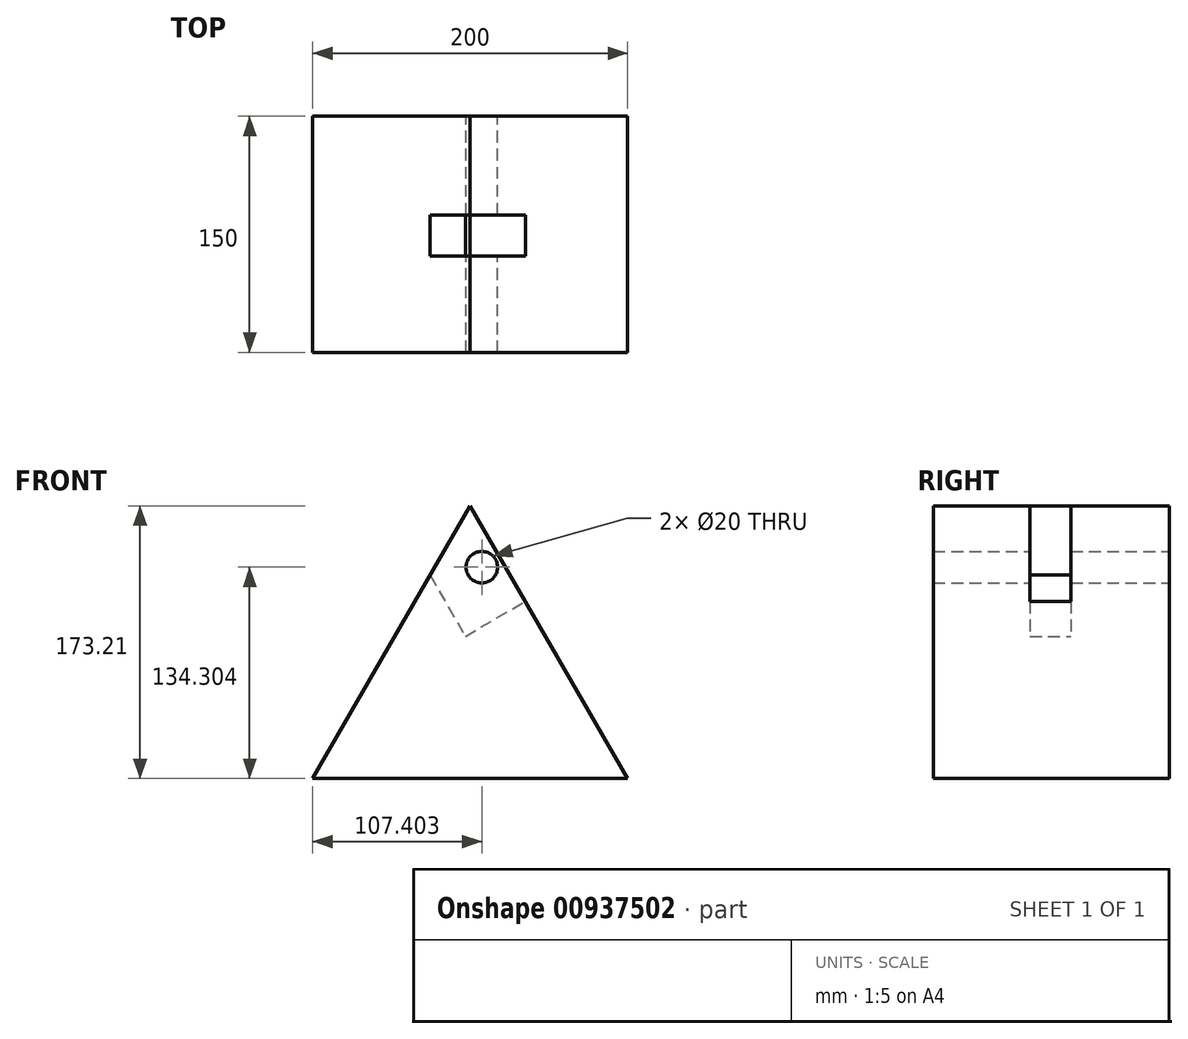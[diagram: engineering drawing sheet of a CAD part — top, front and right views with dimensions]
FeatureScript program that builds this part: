
annotation { "Feature Type Name" : "Feature", "Feature Type Description" : "" }
export const myFeature = defineFeature(function(context is Context, id is Id, definition is map)
    precondition{}
    {
        {
            var Q0;
            Q0=qCreatedBy(makeId("Front.planeOp"),FACE);
            var sketch = newSketch(context, id + "F0", { "sketchPlane" : qUnion([Q0])});
            skLineSegment(sketch, "E0", {"start": v(0, 0) * mm, "end": v(-100, -173.2) * mm});
            skLineSegment(sketch, "E1", {"start": v(-100, -173.2) * mm, "end": v(100, -173.2) * mm});
            skLineSegment(sketch, "E2", {"start": v(100, -173.2) * mm, "end": v(0, 0) * mm});
            skSolve(sketch);
        }
        {
            var Q0;
            Q0=makeQuery(id+"F0.imprint","IMPRINT",FACE,{"disambiguationData":[TD([[makeQuery(id+"F0.imprint","IMPRINT",EDGE,{"derivedFrom":sQuery(id+"F0.wireOp",EDGE,"E0")}),1.0]])]});
            extrude(context, id + "F1", {"entities" : qUnion([Q0]), "depth" : 150 * mm, "offsetDistance" : 25.4 * mm, "symmetric" : true});
        }
        {
            var Q0;
            Q0=makeQuery(id+"F1.opExtrude","CAP_FACE",FACE,{"disambiguationData":[OSD([sQuery(id+"F0.wireOp",EDGE,"E0"),sQuery(id+"F0.wireOp",EDGE,"E1"),sQuery(id+"F0.wireOp",EDGE,"E2")])],"isStart":true});
            var sketch = newSketch(context, id + "F2", { "sketchPlane" : qUnion([Q0])});
            skCircle(sketch, "E3", {"center": v(-7.4, -38.9) * mm, "radius": 10 * mm});
            skSolve(sketch);
        }
        {
            var Q0;
            Q0=makeQuery(id+"F2.imprint","IMPRINT",FACE,{"disambiguationData":[TD([[makeQuery(id+"F2.imprint","IMPRINT",EDGE,{"derivedFrom":sQuery(id+"F2.wireOp",EDGE,"E3")}),1.0]])]});
            extrude(context, id + "F3", {"entities" : qUnion([Q0]), "operationType" : NewBodyOperationType.REMOVE, "endBound" : BoundingType.THROUGH_ALL, "oppositeDirection" : true, "depth" : 25 * mm, "offsetDistance" : 25 * mm});
        }
        {
            var Q0;
            Q0=makeQuery(id+"F1.opExtrude","SWEPT_FACE",FACE,{"disambiguationData":[OSD([sQuery(id+"F0.wireOp",EDGE,"E2")])]});
            var sketch = newSketch(context, id + "F4", { "sketchPlane" : qUnion([Q0])});
            skLineSegment(sketch, "E4.bottom", {"start": v(-13.62, -0.03) * mm, "end": v(12.38, -0.03) * mm});
            skLineSegment(sketch, "E4.top", {"start": v(-13.62, -70.14) * mm, "end": v(12.38, -70.14) * mm});
            skLineSegment(sketch, "E4.left", {"start": v(-13.62, -0.03) * mm, "end": v(-13.62, -70.14) * mm});
            skLineSegment(sketch, "E4.right", {"start": v(12.38, -0.03) * mm, "end": v(12.38, -70.14) * mm});
            skSolve(sketch);
        }
        {
            var Q0;
            Q0=makeQuery(id+"F4.imprint","IMPRINT",FACE,{"disambiguationData":[TD([[makeQuery(id+"F4.imprint","IMPRINT",EDGE,{"derivedFrom":sQuery(id+"F4.wireOp",EDGE,"E4.bottom")}),-1.0]])]});
            extrude(context, id + "F5", {"entities" : qUnion([Q0]), "operationType" : NewBodyOperationType.REMOVE, "oppositeDirection" : true, "depth" : 44 * mm, "offsetDistance" : 25 * mm});
        }
    });
